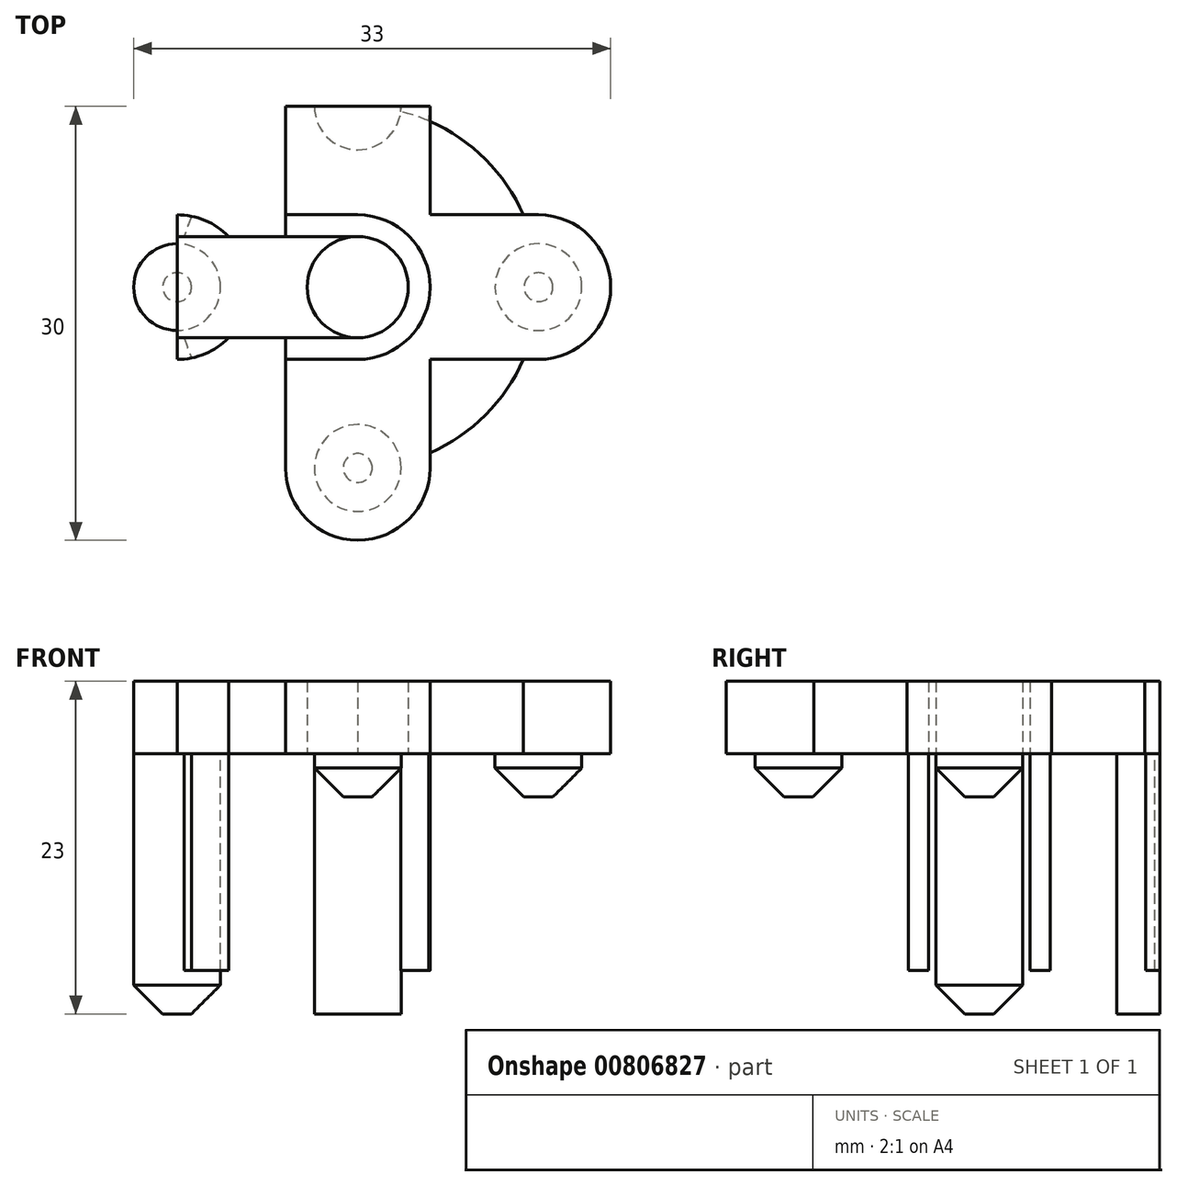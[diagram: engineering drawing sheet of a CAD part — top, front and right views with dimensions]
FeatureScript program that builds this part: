
annotation { "Feature Type Name" : "Feature", "Feature Type Description" : "" }
export const myFeature = defineFeature(function(context is Context, id is Id, definition is map)
    precondition{}
    {
        {
            var Q0;
            Q0=qCreatedBy(makeId("Top.planeOp"),FACE);
            var sketch = newSketch(context, id + "F0", { "sketchPlane" : qUnion([Q0])});
            skCircle(sketch, "E0", {"center": v(0, 0) * mm, "radius": 12.5 * mm});
            skCircle(sketch, "E1", {"center": v(0, 0) * mm, "radius": 3.5 * mm});
            skCircle(sketch, "E2", {"center": v(0, -12.5) * mm, "radius": 5 * mm});
            skCircle(sketch, "E3", {"center": v(0, 12.5) * mm, "radius": 5 * mm});
            skCircle(sketch, "E4", {"center": v(12.5, 0) * mm, "radius": 5 * mm});
            skCircle(sketch, "E5", {"center": v(-12.5, 0) * mm, "radius": 5 * mm});
            skCircle(sketch, "E6", {"center": v(-12.5, 0) * mm, "radius": 3 * mm});
            skCircle(sketch, "E7", {"center": v(0, 12.5) * mm, "radius": 3 * mm});
            skCircle(sketch, "E8", {"center": v(12.5, 0) * mm, "radius": 3 * mm});
            skCircle(sketch, "E9", {"center": v(0, -12.5) * mm, "radius": 3 * mm});
            skCircle(sketch, "E10", {"center": v(0, 0) * mm, "radius": 5 * mm});
            skLineSegment(sketch, "E11.bottom", {"start": v(0, 3.5) * mm, "end": v(-12.5, 3.5) * mm});
            skLineSegment(sketch, "E11.top", {"start": v(0, 5) * mm, "end": v(-12.5, 5) * mm});
            skLineSegment(sketch, "E11.left", {"start": v(0, 3.5) * mm, "end": v(0, 5) * mm});
            skLineSegment(sketch, "E11.right", {"start": v(-12.5, 3.5) * mm, "end": v(-12.5, 5) * mm});
            skLineSegment(sketch, "E12.bottom", {"start": v(0, -3.5) * mm, "end": v(-12.5, -3.5) * mm});
            skLineSegment(sketch, "E12.top", {"start": v(0, -5) * mm, "end": v(-12.5, -5) * mm});
            skLineSegment(sketch, "E12.left", {"start": v(0, -3.5) * mm, "end": v(0, -5) * mm});
            skLineSegment(sketch, "E12.right", {"start": v(-12.5, -3.5) * mm, "end": v(-12.5, -5) * mm});
            skLineSegment(sketch, "E13.bottom", {"start": v(5, 12.5) * mm, "end": v(-5, 12.5) * mm});
            skLineSegment(sketch, "E13.top", {"start": v(5, -12.5) * mm, "end": v(-5, -12.5) * mm});
            skLineSegment(sketch, "E13.left", {"start": v(5, 12.5) * mm, "end": v(5, -12.5) * mm});
            skLineSegment(sketch, "E13.right", {"start": v(-5, 12.5) * mm, "end": v(-5, -12.5) * mm});
            skLineSegment(sketch, "E14.bottom", {"start": v(12.5, 5) * mm, "end": v(-12.5, 5) * mm});
            skLineSegment(sketch, "E14.top", {"start": v(12.5, -5) * mm, "end": v(-12.5, -5) * mm});
            skLineSegment(sketch, "E14.left", {"start": v(12.5, 5) * mm, "end": v(12.5, -5) * mm});
            skLineSegment(sketch, "E14.right", {"start": v(-12.5, 5) * mm, "end": v(-12.5, -5) * mm});
            skSolve(sketch);
        }
        {
            var Q0;
            Q0=qCreatedBy(makeId("Front.planeOp"),FACE);
            var sketch = newSketch(context, id + "F1", { "sketchPlane" : qUnion([Q0])});
            skLineSegment(sketch, "E15", {"start": v(0, 0) * mm, "end": v(0, 10) * mm});
            skLineSegment(sketch, "E16", {"start": v(0, 10) * mm, "end": v(-12.5, 10) * mm});
            skLineSegment(sketch, "E17", {"start": v(-12.5, 10) * mm, "end": v(-12.5, 40) * mm});
            skLineSegment(sketch, "E18", {"start": v(-12.5, 40) * mm, "end": v(0, 10) * mm});
            skSolve(sketch);
        }
        {
            var Q0;
            Q0=makeQuery(id+"F1.imprint","IMPRINT",FACE,{"disambiguationData":[TD([[makeQuery(id+"F1.imprint","IMPRINT",EDGE,{"derivedFrom":sQuery(id+"F1.wireOp",EDGE,"E16")}),-1.0]])]});
            extrude(context, id + "F2", {"entities" : qUnion([Q0]), "endBound" : BoundingType.SYMMETRIC, "depth" : 10 * mm, "offsetDistance" : 25 * mm});
        }
        {
            var Q0;
            {var subQ0=sQuery(id+"F0.wireOp",EDGE,"E11.left");Q0=makeQuery(id+"F0.imprint","IMPRINT",FACE,{"disambiguationData":[TD([[makeQuery(id+"F0.imprint","IMPRINT",EDGE,{"derivedFrom":subQ0}),-1.0]])]});}
            var Q1;
            {var subQ0=sQuery(id+"F0.wireOp",EDGE,"E11.left");Q1=makeQuery(id+"F0.imprint","IMPRINT",FACE,{"disambiguationData":[TD([[makeQuery(id+"F0.imprint","IMPRINT",EDGE,{"derivedFrom":subQ0}),1.0]])]});}
            var Q2;
            {var subQ1=sQuery(id+"F0.wireOp",EDGE,"E10");var subQ3=sQuery(id+"F0.wireOp",EDGE,"E11.bottom");var subQ4=makeQuery(id+"F0.imprint","INTERSECT",VERTEX,{"derivedFrom":[subQ1,subQ3]});Q2=makeQuery(id+"F0.imprint","IMPRINT",FACE,{"disambiguationData":[TD([[makeQuery(id+"F0.imprint","IMPRINT",EDGE,{"disambiguationData":[TD([[subQ4,-1.0]])],"derivedFrom":subQ3}),-1.0]])]});}
            var Q3;
            {var subQ3=sQuery(id+"F0.wireOp",EDGE,"E14.bottom");var subQ7=sQuery(id+"F0.wireOp",EDGE,"E0");var subQ9=makeQuery(id+"F0.imprint","INTERSECT",VERTEX,{"disambiguationData":[OD(1.0)],"derivedFrom":[subQ7,subQ3]});Q3=makeQuery(id+"F0.imprint","IMPRINT",FACE,{"disambiguationData":[TD([[makeQuery(id+"F0.imprint","IMPRINT",EDGE,{"disambiguationData":[TD([[subQ9,-1.0]])],"derivedFrom":subQ7}),1.0]])]});}
            var Q4;
            {var subQ0=sQuery(id+"F0.wireOp",EDGE,"E5");var subQ1=sQuery(id+"F0.wireOp",EDGE,"E0");var subQ2=makeQuery(id+"F0.imprint","INTERSECT",VERTEX,{"disambiguationData":[OD(0.0)],"derivedFrom":[subQ1,subQ0]});Q4=makeQuery(id+"F0.imprint","IMPRINT",FACE,{"disambiguationData":[TD([[makeQuery(id+"F0.imprint","IMPRINT",EDGE,{"disambiguationData":[TD([[subQ2,-1.0]])],"derivedFrom":subQ1}),1.0]])]});}
            var Q5;
            {var subQ0=sQuery(id+"F0.wireOp",EDGE,"E5");var subQ1=sQuery(id+"F0.wireOp",EDGE,"E0");var subQ2=makeQuery(id+"F0.imprint","INTERSECT",VERTEX,{"disambiguationData":[OD(0.0)],"derivedFrom":[subQ1,subQ0]});Q5=makeQuery(id+"F0.imprint","IMPRINT",FACE,{"disambiguationData":[TD([[makeQuery(id+"F0.imprint","IMPRINT",EDGE,{"disambiguationData":[TD([[subQ2,-1.0]])],"derivedFrom":subQ1}),-1.0]])]});}
            var Q6;
            {var subQ0=sQuery(id+"F0.wireOp",EDGE,"E12.bottom");var subQ1=sQuery(id+"F0.wireOp",EDGE,"E0");var subQ2=makeQuery(id+"F0.imprint","INTERSECT",VERTEX,{"derivedFrom":[subQ1,subQ0]});Q6=makeQuery(id+"F0.imprint","IMPRINT",FACE,{"disambiguationData":[TD([[makeQuery(id+"F0.imprint","IMPRINT",EDGE,{"disambiguationData":[TD([[subQ2,-1.0]])],"derivedFrom":subQ1}),-1.0]])]});}
            var Q7;
            {var subQ0=sQuery(id+"F0.wireOp",EDGE,"E12.bottom");var subQ1=sQuery(id+"F0.wireOp",EDGE,"E0");var subQ2=makeQuery(id+"F0.imprint","INTERSECT",VERTEX,{"derivedFrom":[subQ1,subQ0]});Q7=makeQuery(id+"F0.imprint","IMPRINT",FACE,{"disambiguationData":[TD([[makeQuery(id+"F0.imprint","IMPRINT",EDGE,{"disambiguationData":[TD([[subQ2,-1.0]])],"derivedFrom":subQ1}),1.0]])]});}
            var Q8;
            {var subQ5=sQuery(id+"F0.wireOp",EDGE,"E14.top");var subQ7=sQuery(id+"F0.wireOp",EDGE,"E0");var subQ9=makeQuery(id+"F0.imprint","INTERSECT",VERTEX,{"disambiguationData":[OD(0.0)],"derivedFrom":[subQ7,subQ5]});Q8=makeQuery(id+"F0.imprint","IMPRINT",FACE,{"disambiguationData":[TD([[makeQuery(id+"F0.imprint","IMPRINT",EDGE,{"disambiguationData":[TD([[subQ9,1.0]])],"derivedFrom":subQ7}),1.0]])]});}
            var Q9;
            {var subQ1=sQuery(id+"F0.wireOp",EDGE,"E10");var subQ3=sQuery(id+"F0.wireOp",EDGE,"E12.bottom");var subQ4=makeQuery(id+"F0.imprint","INTERSECT",VERTEX,{"derivedFrom":[subQ1,subQ3]});Q9=makeQuery(id+"F0.imprint","IMPRINT",FACE,{"disambiguationData":[TD([[makeQuery(id+"F0.imprint","IMPRINT",EDGE,{"disambiguationData":[TD([[subQ4,-1.0]])],"derivedFrom":subQ3}),1.0]])]});}
            var Q10;
            {var subQ0=sQuery(id+"F0.wireOp",EDGE,"E12.left");Q10=makeQuery(id+"F0.imprint","IMPRINT",FACE,{"disambiguationData":[TD([[makeQuery(id+"F0.imprint","IMPRINT",EDGE,{"derivedFrom":subQ0}),-1.0]])]});}
            var Q11;
            {var subQ0=sQuery(id+"F0.wireOp",EDGE,"E14.top");var subQ1=sQuery(id+"F0.wireOp",EDGE,"E0");var subQ2=makeQuery(id+"F0.imprint","INTERSECT",VERTEX,{"disambiguationData":[OD(0.0)],"derivedFrom":[subQ1,subQ0]});Q11=makeQuery(id+"F0.imprint","IMPRINT",FACE,{"disambiguationData":[TD([[makeQuery(id+"F0.imprint","IMPRINT",EDGE,{"disambiguationData":[TD([[subQ2,1.0]])],"derivedFrom":subQ1}),-1.0]])]});}
            var Q12;
            {var subQ0=sQuery(id+"F0.wireOp",EDGE,"E14.bottom");var subQ1=sQuery(id+"F0.wireOp",EDGE,"E0");var subQ2=makeQuery(id+"F0.imprint","INTERSECT",VERTEX,{"disambiguationData":[OD(1.0)],"derivedFrom":[subQ1,subQ0]});Q12=makeQuery(id+"F0.imprint","IMPRINT",FACE,{"disambiguationData":[TD([[makeQuery(id+"F0.imprint","IMPRINT",EDGE,{"disambiguationData":[TD([[subQ2,-1.0]])],"derivedFrom":subQ1}),-1.0]])]});}
            var Q13;
            {var subQ0=sQuery(id+"F0.wireOp",EDGE,"E14.right");var subQ4=makeQuery(id+"F0.imprint","INTERSECT",VERTEX,{"derivedFrom":[sQuery(id+"F0.wireOp",EDGE,"E0"),subQ0]});Q13=makeQuery(id+"F0.imprint","IMPRINT",FACE,{"disambiguationData":[TD([[makeQuery(id+"F0.imprint","IMPRINT",EDGE,{"disambiguationData":[TD([[subQ4,1.0]])],"derivedFrom":subQ0}),-1.0]])]});}
            var Q14;
            {var subQ0=sQuery(id+"F0.wireOp",EDGE,"E14.right");var subQ1=sQuery(id+"F0.wireOp",EDGE,"E5");var subQ2=makeQuery(id+"F0.imprint","INTERSECT",VERTEX,{"derivedFrom":[subQ1,sQuery(id+"F0.wireOp",EDGE,"E14.bottom"),subQ0]});Q14=makeQuery(id+"F0.imprint","IMPRINT",FACE,{"disambiguationData":[TD([[makeQuery(id+"F0.imprint","IMPRINT",EDGE,{"disambiguationData":[TD([[subQ2,-1.0]])],"derivedFrom":subQ1}),1.0]])]});}
            extrude(context, id + "F3", {"entities" : qUnion([Q0, Q1, Q2, Q3, Q4, Q5, Q6, Q7, Q8, Q9, Q10, Q11, Q12, Q13, Q14]), "operationType" : NewBodyOperationType.ADD, "depth" : 40 * mm, "offsetDistance" : 25 * mm});
        }
        {
            var Q0;
            {var subQ0=sQuery(id+"F0.wireOp",EDGE,"E11.bottom");var subQ3=sQuery(id+"F0.wireOp",EDGE,"E10");var subQ4=makeQuery(id+"F0.imprint","INTERSECT",VERTEX,{"derivedFrom":[subQ3,subQ0]});Q0=makeQuery(id+"F0.imprint","IMPRINT",FACE,{"disambiguationData":[TD([[makeQuery(id+"F0.imprint","IMPRINT",EDGE,{"disambiguationData":[TD([[subQ4,-1.0]])],"derivedFrom":subQ3}),1.0]])]});}
            var Q1;
            {var subQ0=sQuery(id+"F0.wireOp",EDGE,"E11.bottom");var subQ1=sQuery(id+"F0.wireOp",EDGE,"E10");var subQ2=makeQuery(id+"F0.imprint","INTERSECT",VERTEX,{"derivedFrom":[subQ1,subQ0]});Q1=makeQuery(id+"F0.imprint","IMPRINT",FACE,{"disambiguationData":[TD([[makeQuery(id+"F0.imprint","IMPRINT",EDGE,{"disambiguationData":[TD([[subQ2,-1.0]])],"derivedFrom":subQ1}),-1.0]])]});}
            var Q2;
            {var subQ0=sQuery(id+"F0.wireOp",EDGE,"E13.right");var subQ1=sQuery(id+"F0.wireOp",EDGE,"E10");var subQ2=makeQuery(id+"F0.imprint","INTERSECT",VERTEX,{"derivedFrom":[subQ1,subQ0]});Q2=makeQuery(id+"F0.imprint","IMPRINT",FACE,{"disambiguationData":[TD([[makeQuery(id+"F0.imprint","IMPRINT",EDGE,{"disambiguationData":[TD([[subQ2,-1.0]])],"derivedFrom":subQ1}),-1.0]])]});}
            var Q3;
            {var subQ2=sQuery(id+"F0.wireOp",EDGE,"E11.bottom");var subQ5=sQuery(id+"F0.wireOp",EDGE,"E5");var subQ8=makeQuery(id+"F0.imprint","INTERSECT",VERTEX,{"derivedFrom":[subQ5,subQ2]});Q3=makeQuery(id+"F0.imprint","IMPRINT",FACE,{"disambiguationData":[TD([[makeQuery(id+"F0.imprint","IMPRINT",EDGE,{"disambiguationData":[TD([[subQ8,1.0]])],"derivedFrom":subQ5}),-1.0]])]});}
            var Q4;
            {var subQ0=sQuery(id+"F0.wireOp",EDGE,"E11.bottom");var subQ6=sQuery(id+"F0.wireOp",EDGE,"E0");var subQ10=makeQuery(id+"F0.imprint","INTERSECT",VERTEX,{"derivedFrom":[subQ6,subQ0]});Q4=makeQuery(id+"F0.imprint","IMPRINT",FACE,{"disambiguationData":[TD([[makeQuery(id+"F0.imprint","IMPRINT",EDGE,{"disambiguationData":[TD([[subQ10,-1.0]])],"derivedFrom":subQ6}),1.0]])]});}
            var Q5;
            {var subQ0=sQuery(id+"F0.wireOp",EDGE,"E6");var subQ1=sQuery(id+"F0.wireOp",EDGE,"E0");var subQ2=makeQuery(id+"F0.imprint","INTERSECT",VERTEX,{"disambiguationData":[OD(0.0)],"derivedFrom":[subQ1,subQ0]});Q5=makeQuery(id+"F0.imprint","IMPRINT",FACE,{"disambiguationData":[TD([[makeQuery(id+"F0.imprint","IMPRINT",EDGE,{"disambiguationData":[TD([[subQ2,-1.0]])],"derivedFrom":subQ1}),1.0]])]});}
            var Q6;
            {var subQ0=sQuery(id+"F0.wireOp",EDGE,"E6");var subQ1=sQuery(id+"F0.wireOp",EDGE,"E0");var subQ2=makeQuery(id+"F0.imprint","INTERSECT",VERTEX,{"disambiguationData":[OD(0.0)],"derivedFrom":[subQ1,subQ0]});Q6=makeQuery(id+"F0.imprint","IMPRINT",FACE,{"disambiguationData":[TD([[makeQuery(id+"F0.imprint","IMPRINT",EDGE,{"disambiguationData":[TD([[subQ2,-1.0]])],"derivedFrom":subQ1}),-1.0]])]});}
            var Q7;
            {var subQ0=sQuery(id+"F0.wireOp",EDGE,"E14.right");var subQ1=sQuery(id+"F0.wireOp",EDGE,"E0");var subQ2=makeQuery(id+"F0.imprint","INTERSECT",VERTEX,{"derivedFrom":[subQ1,subQ0]});Q7=makeQuery(id+"F0.imprint","IMPRINT",FACE,{"disambiguationData":[TD([[makeQuery(id+"F0.imprint","IMPRINT",EDGE,{"disambiguationData":[TD([[subQ2,-1.0]])],"derivedFrom":subQ1}),-1.0]])]});}
            var Q8;
            {var subQ0=sQuery(id+"F0.wireOp",EDGE,"E13.left");var subQ1=sQuery(id+"F0.wireOp",EDGE,"E0");var subQ2=makeQuery(id+"F0.imprint","INTERSECT",VERTEX,{"disambiguationData":[OD(0.0)],"derivedFrom":[subQ1,subQ0]});Q8=makeQuery(id+"F0.imprint","IMPRINT",FACE,{"disambiguationData":[TD([[makeQuery(id+"F0.imprint","IMPRINT",EDGE,{"disambiguationData":[TD([[subQ2,-1.0]])],"derivedFrom":subQ1}),1.0]])]});}
            var Q9;
            {var subQ0=sQuery(id+"F0.wireOp",EDGE,"E3");var subQ1=sQuery(id+"F0.wireOp",EDGE,"E0");var subQ2=makeQuery(id+"F0.imprint","INTERSECT",VERTEX,{"disambiguationData":[OD(0.0)],"derivedFrom":[subQ1,subQ0]});Q9=makeQuery(id+"F0.imprint","IMPRINT",FACE,{"disambiguationData":[TD([[makeQuery(id+"F0.imprint","IMPRINT",EDGE,{"disambiguationData":[TD([[subQ2,-1.0]])],"derivedFrom":subQ1}),1.0]])]});}
            var Q10;
            {var subQ0=sQuery(id+"F0.wireOp",EDGE,"E7");var subQ1=sQuery(id+"F0.wireOp",EDGE,"E0");var subQ2=makeQuery(id+"F0.imprint","INTERSECT",VERTEX,{"disambiguationData":[OD(0.0)],"derivedFrom":[subQ1,subQ0]});Q10=makeQuery(id+"F0.imprint","IMPRINT",FACE,{"disambiguationData":[TD([[makeQuery(id+"F0.imprint","IMPRINT",EDGE,{"disambiguationData":[TD([[subQ2,-1.0]])],"derivedFrom":subQ1}),1.0]])]});}
            var Q11;
            {var subQ0=sQuery(id+"F0.wireOp",EDGE,"E7");var subQ1=sQuery(id+"F0.wireOp",EDGE,"E0");var subQ2=makeQuery(id+"F0.imprint","INTERSECT",VERTEX,{"disambiguationData":[OD(0.0)],"derivedFrom":[subQ1,subQ0]});Q11=makeQuery(id+"F0.imprint","IMPRINT",FACE,{"disambiguationData":[TD([[makeQuery(id+"F0.imprint","IMPRINT",EDGE,{"disambiguationData":[TD([[subQ2,-1.0]])],"derivedFrom":subQ1}),-1.0]])]});}
            var Q12;
            {var subQ0=sQuery(id+"F0.wireOp",EDGE,"E3");var subQ1=sQuery(id+"F0.wireOp",EDGE,"E0");var subQ2=makeQuery(id+"F0.imprint","INTERSECT",VERTEX,{"disambiguationData":[OD(0.0)],"derivedFrom":[subQ1,subQ0]});Q12=makeQuery(id+"F0.imprint","IMPRINT",FACE,{"disambiguationData":[TD([[makeQuery(id+"F0.imprint","IMPRINT",EDGE,{"disambiguationData":[TD([[subQ2,-1.0]])],"derivedFrom":subQ1}),-1.0]])]});}
            var Q13;
            {var subQ0=sQuery(id+"F0.wireOp",EDGE,"E13.bottom");var subQ4=sQuery(id+"F0.wireOp",EDGE,"E7");var subQ5=makeQuery(id+"F0.imprint","INTERSECT",VERTEX,{"disambiguationData":[OD(0.0)],"derivedFrom":[subQ4,subQ0]});Q13=makeQuery(id+"F0.imprint","IMPRINT",FACE,{"disambiguationData":[TD([[makeQuery(id+"F0.imprint","IMPRINT",EDGE,{"disambiguationData":[TD([[subQ5,1.0]])],"derivedFrom":subQ4}),-1.0]])]});}
            var Q14;
            {var subQ0=sQuery(id+"F0.wireOp",EDGE,"E13.bottom");var subQ1=sQuery(id+"F0.wireOp",EDGE,"E7");var subQ2=makeQuery(id+"F0.imprint","INTERSECT",VERTEX,{"disambiguationData":[OD(0.0)],"derivedFrom":[subQ1,subQ0]});Q14=makeQuery(id+"F0.imprint","IMPRINT",FACE,{"disambiguationData":[TD([[makeQuery(id+"F0.imprint","IMPRINT",EDGE,{"disambiguationData":[TD([[subQ2,1.0]])],"derivedFrom":subQ1}),1.0]])]});}
            var Q15;
            {var subQ0=sQuery(id+"F0.wireOp",EDGE,"E13.bottom");var subQ1=sQuery(id+"F0.wireOp",EDGE,"E0");var subQ2=makeQuery(id+"F0.imprint","INTERSECT",VERTEX,{"derivedFrom":[subQ1,subQ0]});Q15=makeQuery(id+"F0.imprint","IMPRINT",FACE,{"disambiguationData":[TD([[makeQuery(id+"F0.imprint","IMPRINT",EDGE,{"disambiguationData":[TD([[subQ2,-1.0]])],"derivedFrom":subQ1}),-1.0]])]});}
            var Q16;
            {var subQ0=sQuery(id+"F0.wireOp",EDGE,"E7");var subQ1=sQuery(id+"F0.wireOp",EDGE,"E0");var subQ2=makeQuery(id+"F0.imprint","INTERSECT",VERTEX,{"disambiguationData":[OD(1.0)],"derivedFrom":[subQ1,subQ0]});Q16=makeQuery(id+"F0.imprint","IMPRINT",FACE,{"disambiguationData":[TD([[makeQuery(id+"F0.imprint","IMPRINT",EDGE,{"disambiguationData":[TD([[subQ2,-1.0]])],"derivedFrom":subQ1}),-1.0]])]});}
            var Q17;
            {var subQ0=sQuery(id+"F0.wireOp",EDGE,"E8");var subQ1=sQuery(id+"F0.wireOp",EDGE,"E0");var subQ2=makeQuery(id+"F0.imprint","INTERSECT",VERTEX,{"disambiguationData":[OD(0.0)],"derivedFrom":[subQ1,subQ0]});Q17=makeQuery(id+"F0.imprint","IMPRINT",FACE,{"disambiguationData":[TD([[makeQuery(id+"F0.imprint","IMPRINT",EDGE,{"disambiguationData":[TD([[subQ2,-1.0]])],"derivedFrom":subQ1}),1.0]])]});}
            var Q18;
            {var subQ0=sQuery(id+"F0.wireOp",EDGE,"E8");var subQ1=sQuery(id+"F0.wireOp",EDGE,"E0");var subQ2=makeQuery(id+"F0.imprint","INTERSECT",VERTEX,{"disambiguationData":[OD(0.0)],"derivedFrom":[subQ1,subQ0]});Q18=makeQuery(id+"F0.imprint","IMPRINT",FACE,{"disambiguationData":[TD([[makeQuery(id+"F0.imprint","IMPRINT",EDGE,{"disambiguationData":[TD([[subQ2,-1.0]])],"derivedFrom":subQ1}),-1.0]])]});}
            var Q19;
            {var subQ0=sQuery(id+"F0.wireOp",EDGE,"E14.left");var subQ4=sQuery(id+"F0.wireOp",EDGE,"E8");var subQ5=makeQuery(id+"F0.imprint","INTERSECT",VERTEX,{"disambiguationData":[OD(0.0)],"derivedFrom":[subQ4,subQ0]});Q19=makeQuery(id+"F0.imprint","IMPRINT",FACE,{"disambiguationData":[TD([[makeQuery(id+"F0.imprint","IMPRINT",EDGE,{"disambiguationData":[TD([[subQ5,1.0]])],"derivedFrom":subQ4}),-1.0]])]});}
            var Q20;
            {var subQ0=sQuery(id+"F0.wireOp",EDGE,"E14.left");var subQ1=sQuery(id+"F0.wireOp",EDGE,"E8");var subQ2=makeQuery(id+"F0.imprint","INTERSECT",VERTEX,{"disambiguationData":[OD(0.0)],"derivedFrom":[subQ1,subQ0]});Q20=makeQuery(id+"F0.imprint","IMPRINT",FACE,{"disambiguationData":[TD([[makeQuery(id+"F0.imprint","IMPRINT",EDGE,{"disambiguationData":[TD([[subQ2,1.0]])],"derivedFrom":subQ1}),1.0]])]});}
            var Q21;
            {var subQ0=sQuery(id+"F0.wireOp",EDGE,"E8");var subQ1=sQuery(id+"F0.wireOp",EDGE,"E0");var subQ2=makeQuery(id+"F0.imprint","INTERSECT",VERTEX,{"disambiguationData":[OD(0.0)],"derivedFrom":[subQ1,subQ0]});Q21=makeQuery(id+"F0.imprint","IMPRINT",FACE,{"disambiguationData":[TD([[makeQuery(id+"F0.imprint","IMPRINT",EDGE,{"disambiguationData":[TD([[subQ2,1.0]])],"derivedFrom":subQ1}),1.0]])]});}
            var Q22;
            {var subQ0=sQuery(id+"F0.wireOp",EDGE,"E8");var subQ1=sQuery(id+"F0.wireOp",EDGE,"E0");var subQ2=makeQuery(id+"F0.imprint","INTERSECT",VERTEX,{"disambiguationData":[OD(0.0)],"derivedFrom":[subQ1,subQ0]});Q22=makeQuery(id+"F0.imprint","IMPRINT",FACE,{"disambiguationData":[TD([[makeQuery(id+"F0.imprint","IMPRINT",EDGE,{"disambiguationData":[TD([[subQ2,1.0]])],"derivedFrom":subQ1}),-1.0]])]});}
            var Q23;
            {var subQ0=sQuery(id+"F0.wireOp",EDGE,"E14.left");var subQ1=sQuery(id+"F0.wireOp",EDGE,"E0");var subQ2=makeQuery(id+"F0.imprint","INTERSECT",VERTEX,{"derivedFrom":[subQ1,subQ0]});Q23=makeQuery(id+"F0.imprint","IMPRINT",FACE,{"disambiguationData":[TD([[makeQuery(id+"F0.imprint","IMPRINT",EDGE,{"disambiguationData":[TD([[subQ2,1.0]])],"derivedFrom":subQ1}),-1.0]])]});}
            var Q24;
            {var subQ0=sQuery(id+"F0.wireOp",EDGE,"E4");var subQ1=sQuery(id+"F0.wireOp",EDGE,"E0");var subQ2=makeQuery(id+"F0.imprint","INTERSECT",VERTEX,{"disambiguationData":[OD(1.0)],"derivedFrom":[subQ1,subQ0]});Q24=makeQuery(id+"F0.imprint","IMPRINT",FACE,{"disambiguationData":[TD([[makeQuery(id+"F0.imprint","IMPRINT",EDGE,{"disambiguationData":[TD([[subQ2,-1.0]])],"derivedFrom":subQ1}),-1.0]])]});}
            var Q25;
            {var subQ2=sQuery(id+"F0.wireOp",EDGE,"E14.bottom");var subQ5=sQuery(id+"F0.wireOp",EDGE,"E0");var subQ8=makeQuery(id+"F0.imprint","INTERSECT",VERTEX,{"disambiguationData":[OD(0.0)],"derivedFrom":[subQ5,subQ2]});Q25=makeQuery(id+"F0.imprint","IMPRINT",FACE,{"disambiguationData":[TD([[makeQuery(id+"F0.imprint","IMPRINT",EDGE,{"disambiguationData":[TD([[subQ8,1.0]])],"derivedFrom":subQ5}),1.0]])]});}
            var Q26;
            {var subQ0=sQuery(id+"F0.wireOp",EDGE,"E13.left");var subQ1=sQuery(id+"F0.wireOp",EDGE,"E0");var subQ2=makeQuery(id+"F0.imprint","INTERSECT",VERTEX,{"disambiguationData":[OD(0.0)],"derivedFrom":[subQ1,subQ0]});Q26=makeQuery(id+"F0.imprint","IMPRINT",FACE,{"disambiguationData":[TD([[makeQuery(id+"F0.imprint","IMPRINT",EDGE,{"disambiguationData":[TD([[subQ2,-1.0]])],"derivedFrom":subQ1}),-1.0]])]});}
            var Q27;
            {var subQ0=sQuery(id+"F0.wireOp",EDGE,"E13.right");var subQ1=sQuery(id+"F0.wireOp",EDGE,"E0");var subQ2=makeQuery(id+"F0.imprint","INTERSECT",VERTEX,{"disambiguationData":[OD(0.0)],"derivedFrom":[subQ1,subQ0]});Q27=makeQuery(id+"F0.imprint","IMPRINT",FACE,{"disambiguationData":[TD([[makeQuery(id+"F0.imprint","IMPRINT",EDGE,{"disambiguationData":[TD([[subQ2,1.0]])],"derivedFrom":subQ1}),-1.0]])]});}
            var Q28;
            {var subQ0=sQuery(id+"F0.wireOp",EDGE,"E14.bottom");var subQ1=sQuery(id+"F0.wireOp",EDGE,"E0");var subQ2=makeQuery(id+"F0.imprint","INTERSECT",VERTEX,{"disambiguationData":[OD(0.0)],"derivedFrom":[subQ1,subQ0]});Q28=makeQuery(id+"F0.imprint","IMPRINT",FACE,{"disambiguationData":[TD([[makeQuery(id+"F0.imprint","IMPRINT",EDGE,{"disambiguationData":[TD([[subQ2,1.0]])],"derivedFrom":subQ1}),-1.0]])]});}
            var Q29;
            {var subQ0=sQuery(id+"F0.wireOp",EDGE,"E14.top");var subQ1=sQuery(id+"F0.wireOp",EDGE,"E0");var subQ2=makeQuery(id+"F0.imprint","INTERSECT",VERTEX,{"disambiguationData":[OD(1.0)],"derivedFrom":[subQ1,subQ0]});Q29=makeQuery(id+"F0.imprint","IMPRINT",FACE,{"disambiguationData":[TD([[makeQuery(id+"F0.imprint","IMPRINT",EDGE,{"disambiguationData":[TD([[subQ2,-1.0]])],"derivedFrom":subQ1}),-1.0]])]});}
            var Q30;
            {var subQ0=sQuery(id+"F0.wireOp",EDGE,"E13.top");var subQ4=sQuery(id+"F0.wireOp",EDGE,"E9");var subQ5=makeQuery(id+"F0.imprint","INTERSECT",VERTEX,{"disambiguationData":[OD(0.0)],"derivedFrom":[subQ4,subQ0]});Q30=makeQuery(id+"F0.imprint","IMPRINT",FACE,{"disambiguationData":[TD([[makeQuery(id+"F0.imprint","IMPRINT",EDGE,{"disambiguationData":[TD([[subQ5,1.0]])],"derivedFrom":subQ4}),-1.0]])]});}
            var Q31;
            {var subQ0=sQuery(id+"F0.wireOp",EDGE,"E13.top");var subQ1=sQuery(id+"F0.wireOp",EDGE,"E0");var subQ2=makeQuery(id+"F0.imprint","INTERSECT",VERTEX,{"derivedFrom":[subQ1,subQ0]});Q31=makeQuery(id+"F0.imprint","IMPRINT",FACE,{"disambiguationData":[TD([[makeQuery(id+"F0.imprint","IMPRINT",EDGE,{"disambiguationData":[TD([[subQ2,-1.0]])],"derivedFrom":subQ1}),-1.0]])]});}
            var Q32;
            {var subQ0=sQuery(id+"F0.wireOp",EDGE,"E9");var subQ1=sQuery(id+"F0.wireOp",EDGE,"E0");var subQ2=makeQuery(id+"F0.imprint","INTERSECT",VERTEX,{"disambiguationData":[OD(1.0)],"derivedFrom":[subQ1,subQ0]});Q32=makeQuery(id+"F0.imprint","IMPRINT",FACE,{"disambiguationData":[TD([[makeQuery(id+"F0.imprint","IMPRINT",EDGE,{"disambiguationData":[TD([[subQ2,-1.0]])],"derivedFrom":subQ1}),-1.0]])]});}
            var Q33;
            {var subQ0=sQuery(id+"F0.wireOp",EDGE,"E13.top");var subQ1=sQuery(id+"F0.wireOp",EDGE,"E9");var subQ2=makeQuery(id+"F0.imprint","INTERSECT",VERTEX,{"disambiguationData":[OD(0.0)],"derivedFrom":[subQ1,subQ0]});Q33=makeQuery(id+"F0.imprint","IMPRINT",FACE,{"disambiguationData":[TD([[makeQuery(id+"F0.imprint","IMPRINT",EDGE,{"disambiguationData":[TD([[subQ2,1.0]])],"derivedFrom":subQ1}),1.0]])]});}
            var Q34;
            {var subQ0=sQuery(id+"F0.wireOp",EDGE,"E9");var subQ1=sQuery(id+"F0.wireOp",EDGE,"E0");var subQ2=makeQuery(id+"F0.imprint","INTERSECT",VERTEX,{"disambiguationData":[OD(0.0)],"derivedFrom":[subQ1,subQ0]});Q34=makeQuery(id+"F0.imprint","IMPRINT",FACE,{"disambiguationData":[TD([[makeQuery(id+"F0.imprint","IMPRINT",EDGE,{"disambiguationData":[TD([[subQ2,-1.0]])],"derivedFrom":subQ1}),1.0]])]});}
            var Q35;
            {var subQ0=sQuery(id+"F0.wireOp",EDGE,"E2");var subQ1=sQuery(id+"F0.wireOp",EDGE,"E0");var subQ2=makeQuery(id+"F0.imprint","INTERSECT",VERTEX,{"disambiguationData":[OD(0.0)],"derivedFrom":[subQ1,subQ0]});Q35=makeQuery(id+"F0.imprint","IMPRINT",FACE,{"disambiguationData":[TD([[makeQuery(id+"F0.imprint","IMPRINT",EDGE,{"disambiguationData":[TD([[subQ2,-1.0]])],"derivedFrom":subQ1}),1.0]])]});}
            var Q36;
            {var subQ0=sQuery(id+"F0.wireOp",EDGE,"E2");var subQ1=sQuery(id+"F0.wireOp",EDGE,"E0");var subQ2=makeQuery(id+"F0.imprint","INTERSECT",VERTEX,{"disambiguationData":[OD(0.0)],"derivedFrom":[subQ1,subQ0]});Q36=makeQuery(id+"F0.imprint","IMPRINT",FACE,{"disambiguationData":[TD([[makeQuery(id+"F0.imprint","IMPRINT",EDGE,{"disambiguationData":[TD([[subQ2,-1.0]])],"derivedFrom":subQ1}),-1.0]])]});}
            var Q37;
            {var subQ0=sQuery(id+"F0.wireOp",EDGE,"E9");var subQ1=sQuery(id+"F0.wireOp",EDGE,"E0");var subQ2=makeQuery(id+"F0.imprint","INTERSECT",VERTEX,{"disambiguationData":[OD(0.0)],"derivedFrom":[subQ1,subQ0]});Q37=makeQuery(id+"F0.imprint","IMPRINT",FACE,{"disambiguationData":[TD([[makeQuery(id+"F0.imprint","IMPRINT",EDGE,{"disambiguationData":[TD([[subQ2,-1.0]])],"derivedFrom":subQ1}),-1.0]])]});}
            var Q38;
            {var subQ1=sQuery(id+"F0.wireOp",EDGE,"E0");var subQ8=sQuery(id+"F0.wireOp",EDGE,"E13.right");var subQ9=makeQuery(id+"F0.imprint","INTERSECT",VERTEX,{"disambiguationData":[OD(1.0)],"derivedFrom":[subQ1,subQ8]});Q38=makeQuery(id+"F0.imprint","IMPRINT",FACE,{"disambiguationData":[TD([[makeQuery(id+"F0.imprint","IMPRINT",EDGE,{"disambiguationData":[TD([[subQ9,-1.0]])],"derivedFrom":subQ1}),1.0]])]});}
            var Q39;
            {var subQ0=sQuery(id+"F0.wireOp",EDGE,"E13.left");var subQ1=sQuery(id+"F0.wireOp",EDGE,"E0");var subQ2=makeQuery(id+"F0.imprint","INTERSECT",VERTEX,{"disambiguationData":[OD(1.0)],"derivedFrom":[subQ1,subQ0]});Q39=makeQuery(id+"F0.imprint","IMPRINT",FACE,{"disambiguationData":[TD([[makeQuery(id+"F0.imprint","IMPRINT",EDGE,{"disambiguationData":[TD([[subQ2,1.0]])],"derivedFrom":subQ1}),-1.0]])]});}
            var Q40;
            {var subQ0=sQuery(id+"F0.wireOp",EDGE,"E13.right");var subQ1=sQuery(id+"F0.wireOp",EDGE,"E0");var subQ2=makeQuery(id+"F0.imprint","INTERSECT",VERTEX,{"disambiguationData":[OD(1.0)],"derivedFrom":[subQ1,subQ0]});Q40=makeQuery(id+"F0.imprint","IMPRINT",FACE,{"disambiguationData":[TD([[makeQuery(id+"F0.imprint","IMPRINT",EDGE,{"disambiguationData":[TD([[subQ2,-1.0]])],"derivedFrom":subQ1}),-1.0]])]});}
            var Q41;
            {var subQ1=sQuery(id+"F0.wireOp",EDGE,"E10");var subQ3=sQuery(id+"F0.wireOp",EDGE,"E13.left");var subQ4=makeQuery(id+"F0.imprint","INTERSECT",VERTEX,{"derivedFrom":[subQ1,subQ3]});Q41=makeQuery(id+"F0.imprint","IMPRINT",FACE,{"disambiguationData":[TD([[makeQuery(id+"F0.imprint","IMPRINT",EDGE,{"disambiguationData":[TD([[subQ4,1.0]])],"derivedFrom":subQ3}),-1.0]])]});}
            var Q42;
            {var subQ1=sQuery(id+"F0.wireOp",EDGE,"E10");var subQ3=sQuery(id+"F0.wireOp",EDGE,"E13.left");var subQ4=makeQuery(id+"F0.imprint","INTERSECT",VERTEX,{"derivedFrom":[subQ1,subQ3]});Q42=makeQuery(id+"F0.imprint","IMPRINT",FACE,{"disambiguationData":[TD([[makeQuery(id+"F0.imprint","IMPRINT",EDGE,{"disambiguationData":[TD([[subQ4,-1.0]])],"derivedFrom":subQ3}),-1.0]])]});}
            var Q43;
            {var subQ0=sQuery(id+"F0.wireOp",EDGE,"E6");var subQ1=sQuery(id+"F0.wireOp",EDGE,"E0");var subQ2=makeQuery(id+"F0.imprint","INTERSECT",VERTEX,{"disambiguationData":[OD(1.0)],"derivedFrom":[subQ1,subQ0]});Q43=makeQuery(id+"F0.imprint","IMPRINT",FACE,{"disambiguationData":[TD([[makeQuery(id+"F0.imprint","IMPRINT",EDGE,{"disambiguationData":[TD([[subQ2,-1.0]])],"derivedFrom":subQ1}),-1.0]])]});}
            var Q44;
            {var subQ0=sQuery(id+"F0.wireOp",EDGE,"E11.bottom");var subQ1=sQuery(id+"F0.wireOp",EDGE,"E0");var subQ2=makeQuery(id+"F0.imprint","INTERSECT",VERTEX,{"derivedFrom":[subQ1,subQ0]});Q44=makeQuery(id+"F0.imprint","IMPRINT",FACE,{"disambiguationData":[TD([[makeQuery(id+"F0.imprint","IMPRINT",EDGE,{"disambiguationData":[TD([[subQ2,-1.0]])],"derivedFrom":subQ1}),-1.0]])]});}
            extrude(context, id + "F4", {"entities" : qUnion([Q0, Q1, Q2, Q3, Q4, Q5, Q6, Q7, Q8, Q9, Q10, Q11, Q12, Q13, Q14, Q15, Q16, Q17, Q18, Q19, Q20, Q21, Q22, Q23, Q24, Q25, Q26, Q27, Q28, Q29, Q30, Q31, Q32, Q33, Q34, Q35, Q36, Q37, Q38, Q39, Q40, Q41, Q42, Q43, Q44]), "depth" : 10 * mm, "offsetDistance" : 25 * mm});
        }
        {
            var Q0;
            {var subQ0=sQuery(id+"F0.wireOp",EDGE,"E1");var subQ1=makeQuery(id+"F0.imprint","INTERSECT",VERTEX,{"derivedFrom":[subQ0,sQuery(id+"F0.wireOp",EDGE,"E11.bottom"),sQuery(id+"F0.wireOp",EDGE,"E11.left")]});Q0=makeQuery(id+"F0.imprint","IMPRINT",FACE,{"disambiguationData":[TD([[makeQuery(id+"F0.imprint","IMPRINT",EDGE,{"disambiguationData":[TD([[subQ1,-1.0]])],"derivedFrom":subQ0}),1.0]])]});}
            extrude(context, id + "F5", {"entities" : qUnion([Q0]), "operationType" : NewBodyOperationType.REMOVE, "oppositeDirection" : true, "depth" : -40 * mm, "offsetDistance" : 25 * mm});
        }
        {
            var Q0;
            {var subQ0=sQuery(id+"F0.wireOp",EDGE,"E14.right");var subQ1=sQuery(id+"F0.wireOp",EDGE,"E5");var subQ2=makeQuery(id+"F0.imprint","INTERSECT",VERTEX,{"derivedFrom":[subQ1,sQuery(id+"F0.wireOp",EDGE,"E14.bottom"),subQ0]});Q0=makeQuery(id+"F0.imprint","IMPRINT",FACE,{"disambiguationData":[TD([[makeQuery(id+"F0.imprint","IMPRINT",EDGE,{"disambiguationData":[TD([[subQ2,-1.0]])],"derivedFrom":subQ1}),1.0]])]});}
            var Q1;
            {var subQ0=sQuery(id+"F0.wireOp",EDGE,"E13.bottom");var subQ4=sQuery(id+"F0.wireOp",EDGE,"E7");var subQ5=makeQuery(id+"F0.imprint","INTERSECT",VERTEX,{"disambiguationData":[OD(0.0)],"derivedFrom":[subQ4,subQ0]});Q1=makeQuery(id+"F0.imprint","IMPRINT",FACE,{"disambiguationData":[TD([[makeQuery(id+"F0.imprint","IMPRINT",EDGE,{"disambiguationData":[TD([[subQ5,1.0]])],"derivedFrom":subQ4}),-1.0]])]});}
            extrude(context, id + "F6", {"entities" : qUnion([Q0, Q1]), "oppositeDirection" : true, "depth" : 15 * mm, "offsetDistance" : 25 * mm});
        }
        {
            var Q0;
            {var subQ0=sQuery(id+"F0.wireOp",EDGE,"E14.right");var subQ4=makeQuery(id+"F0.imprint","INTERSECT",VERTEX,{"derivedFrom":[sQuery(id+"F0.wireOp",EDGE,"E0"),subQ0]});Q0=makeQuery(id+"F0.imprint","IMPRINT",FACE,{"disambiguationData":[TD([[makeQuery(id+"F0.imprint","IMPRINT",EDGE,{"disambiguationData":[TD([[subQ4,1.0]])],"derivedFrom":subQ0}),-1.0]])]});}
            var Q1;
            {var subQ0=sQuery(id+"F0.wireOp",EDGE,"E14.right");var subQ1=sQuery(id+"F0.wireOp",EDGE,"E0");var subQ2=makeQuery(id+"F0.imprint","INTERSECT",VERTEX,{"derivedFrom":[subQ1,subQ0]});Q1=makeQuery(id+"F0.imprint","IMPRINT",FACE,{"disambiguationData":[TD([[makeQuery(id+"F0.imprint","IMPRINT",EDGE,{"disambiguationData":[TD([[subQ2,-1.0]])],"derivedFrom":subQ1}),-1.0]])]});}
            var Q2;
            {var subQ0=sQuery(id+"F0.wireOp",EDGE,"E6");var subQ1=sQuery(id+"F0.wireOp",EDGE,"E0");var subQ2=makeQuery(id+"F0.imprint","INTERSECT",VERTEX,{"disambiguationData":[OD(0.0)],"derivedFrom":[subQ1,subQ0]});Q2=makeQuery(id+"F0.imprint","IMPRINT",FACE,{"disambiguationData":[TD([[makeQuery(id+"F0.imprint","IMPRINT",EDGE,{"disambiguationData":[TD([[subQ2,-1.0]])],"derivedFrom":subQ1}),1.0]])]});}
            var Q3;
            {var subQ0=sQuery(id+"F0.wireOp",EDGE,"E6");var subQ1=sQuery(id+"F0.wireOp",EDGE,"E0");var subQ2=makeQuery(id+"F0.imprint","INTERSECT",VERTEX,{"disambiguationData":[OD(0.0)],"derivedFrom":[subQ1,subQ0]});Q3=makeQuery(id+"F0.imprint","IMPRINT",FACE,{"disambiguationData":[TD([[makeQuery(id+"F0.imprint","IMPRINT",EDGE,{"disambiguationData":[TD([[subQ2,-1.0]])],"derivedFrom":subQ1}),-1.0]])]});}
            var Q4;
            {var subQ0=sQuery(id+"F0.wireOp",EDGE,"E7");var subQ1=sQuery(id+"F0.wireOp",EDGE,"E0");var subQ2=makeQuery(id+"F0.imprint","INTERSECT",VERTEX,{"disambiguationData":[OD(0.0)],"derivedFrom":[subQ1,subQ0]});Q4=makeQuery(id+"F0.imprint","IMPRINT",FACE,{"disambiguationData":[TD([[makeQuery(id+"F0.imprint","IMPRINT",EDGE,{"disambiguationData":[TD([[subQ2,-1.0]])],"derivedFrom":subQ1}),1.0]])]});}
            var Q5;
            {var subQ0=sQuery(id+"F0.wireOp",EDGE,"E7");var subQ1=sQuery(id+"F0.wireOp",EDGE,"E0");var subQ2=makeQuery(id+"F0.imprint","INTERSECT",VERTEX,{"disambiguationData":[OD(0.0)],"derivedFrom":[subQ1,subQ0]});Q5=makeQuery(id+"F0.imprint","IMPRINT",FACE,{"disambiguationData":[TD([[makeQuery(id+"F0.imprint","IMPRINT",EDGE,{"disambiguationData":[TD([[subQ2,-1.0]])],"derivedFrom":subQ1}),-1.0]])]});}
            var Q6;
            {var subQ0=sQuery(id+"F0.wireOp",EDGE,"E13.bottom");var subQ1=sQuery(id+"F0.wireOp",EDGE,"E0");var subQ2=makeQuery(id+"F0.imprint","INTERSECT",VERTEX,{"derivedFrom":[subQ1,subQ0]});Q6=makeQuery(id+"F0.imprint","IMPRINT",FACE,{"disambiguationData":[TD([[makeQuery(id+"F0.imprint","IMPRINT",EDGE,{"disambiguationData":[TD([[subQ2,-1.0]])],"derivedFrom":subQ1}),-1.0]])]});}
            var Q7;
            {var subQ0=sQuery(id+"F0.wireOp",EDGE,"E13.bottom");var subQ1=sQuery(id+"F0.wireOp",EDGE,"E7");var subQ2=makeQuery(id+"F0.imprint","INTERSECT",VERTEX,{"disambiguationData":[OD(0.0)],"derivedFrom":[subQ1,subQ0]});Q7=makeQuery(id+"F0.imprint","IMPRINT",FACE,{"disambiguationData":[TD([[makeQuery(id+"F0.imprint","IMPRINT",EDGE,{"disambiguationData":[TD([[subQ2,1.0]])],"derivedFrom":subQ1}),1.0]])]});}
            extrude(context, id + "F7", {"entities" : qUnion([Q0, Q1, Q2, Q3, Q4, Q5, Q6, Q7]), "oppositeDirection" : true, "depth" : 18 * mm, "offsetDistance" : 25 * mm});
        }
        {
            var Q0;
            Q0=makeQuery(id+"F7.opExtrude","CAP_FACE",FACE,{"disambiguationData":[OSD([sQuery(id+"F0.wireOp",EDGE,"E6")])],"isStart":false});
            var Q1;
            Q1=makeQuery(id+"F7.opExtrude","CAP_FACE",FACE,{"disambiguationData":[OSD([sQuery(id+"F0.wireOp",EDGE,"E7")])],"isStart":false});
            chamfer(context, id + "F8", {"entities" : qUnion([Q0, Q1]), "width" : 2 * mm, "tangentPropagation" : true});
        }
        {
            var Q0;
            {var subQ0=sQuery(id+"F0.wireOp",EDGE,"E14.left");var subQ1=sQuery(id+"F0.wireOp",EDGE,"E0");var subQ2=makeQuery(id+"F0.imprint","INTERSECT",VERTEX,{"derivedFrom":[subQ1,subQ0]});Q0=makeQuery(id+"F0.imprint","IMPRINT",FACE,{"disambiguationData":[TD([[makeQuery(id+"F0.imprint","IMPRINT",EDGE,{"disambiguationData":[TD([[subQ2,1.0]])],"derivedFrom":subQ1}),-1.0]])]});}
            var Q1;
            {var subQ0=sQuery(id+"F0.wireOp",EDGE,"E8");var subQ1=sQuery(id+"F0.wireOp",EDGE,"E0");var subQ2=makeQuery(id+"F0.imprint","INTERSECT",VERTEX,{"disambiguationData":[OD(0.0)],"derivedFrom":[subQ1,subQ0]});Q1=makeQuery(id+"F0.imprint","IMPRINT",FACE,{"disambiguationData":[TD([[makeQuery(id+"F0.imprint","IMPRINT",EDGE,{"disambiguationData":[TD([[subQ2,1.0]])],"derivedFrom":subQ1}),1.0]])]});}
            var Q2;
            {var subQ0=sQuery(id+"F0.wireOp",EDGE,"E8");var subQ1=sQuery(id+"F0.wireOp",EDGE,"E0");var subQ2=makeQuery(id+"F0.imprint","INTERSECT",VERTEX,{"disambiguationData":[OD(0.0)],"derivedFrom":[subQ1,subQ0]});Q2=makeQuery(id+"F0.imprint","IMPRINT",FACE,{"disambiguationData":[TD([[makeQuery(id+"F0.imprint","IMPRINT",EDGE,{"disambiguationData":[TD([[subQ2,1.0]])],"derivedFrom":subQ1}),-1.0]])]});}
            var Q3;
            {var subQ0=sQuery(id+"F0.wireOp",EDGE,"E14.left");var subQ1=sQuery(id+"F0.wireOp",EDGE,"E8");var subQ2=makeQuery(id+"F0.imprint","INTERSECT",VERTEX,{"disambiguationData":[OD(0.0)],"derivedFrom":[subQ1,subQ0]});Q3=makeQuery(id+"F0.imprint","IMPRINT",FACE,{"disambiguationData":[TD([[makeQuery(id+"F0.imprint","IMPRINT",EDGE,{"disambiguationData":[TD([[subQ2,1.0]])],"derivedFrom":subQ1}),1.0]])]});}
            var Q4;
            {var subQ0=sQuery(id+"F0.wireOp",EDGE,"E13.top");var subQ1=sQuery(id+"F0.wireOp",EDGE,"E9");var subQ2=makeQuery(id+"F0.imprint","INTERSECT",VERTEX,{"disambiguationData":[OD(0.0)],"derivedFrom":[subQ1,subQ0]});Q4=makeQuery(id+"F0.imprint","IMPRINT",FACE,{"disambiguationData":[TD([[makeQuery(id+"F0.imprint","IMPRINT",EDGE,{"disambiguationData":[TD([[subQ2,1.0]])],"derivedFrom":subQ1}),1.0]])]});}
            var Q5;
            {var subQ0=sQuery(id+"F0.wireOp",EDGE,"E9");var subQ1=sQuery(id+"F0.wireOp",EDGE,"E0");var subQ2=makeQuery(id+"F0.imprint","INTERSECT",VERTEX,{"disambiguationData":[OD(0.0)],"derivedFrom":[subQ1,subQ0]});Q5=makeQuery(id+"F0.imprint","IMPRINT",FACE,{"disambiguationData":[TD([[makeQuery(id+"F0.imprint","IMPRINT",EDGE,{"disambiguationData":[TD([[subQ2,-1.0]])],"derivedFrom":subQ1}),1.0]])]});}
            var Q6;
            {var subQ0=sQuery(id+"F0.wireOp",EDGE,"E13.top");var subQ1=sQuery(id+"F0.wireOp",EDGE,"E0");var subQ2=makeQuery(id+"F0.imprint","INTERSECT",VERTEX,{"derivedFrom":[subQ1,subQ0]});Q6=makeQuery(id+"F0.imprint","IMPRINT",FACE,{"disambiguationData":[TD([[makeQuery(id+"F0.imprint","IMPRINT",EDGE,{"disambiguationData":[TD([[subQ2,-1.0]])],"derivedFrom":subQ1}),-1.0]])]});}
            var Q7;
            {var subQ0=sQuery(id+"F0.wireOp",EDGE,"E9");var subQ1=sQuery(id+"F0.wireOp",EDGE,"E0");var subQ2=makeQuery(id+"F0.imprint","INTERSECT",VERTEX,{"disambiguationData":[OD(0.0)],"derivedFrom":[subQ1,subQ0]});Q7=makeQuery(id+"F0.imprint","IMPRINT",FACE,{"disambiguationData":[TD([[makeQuery(id+"F0.imprint","IMPRINT",EDGE,{"disambiguationData":[TD([[subQ2,-1.0]])],"derivedFrom":subQ1}),-1.0]])]});}
            extrude(context, id + "F9", {"entities" : qUnion([Q0, Q1, Q2, Q3, Q4, Q5, Q6, Q7]), "operationType" : NewBodyOperationType.ADD, "oppositeDirection" : true, "depth" : 3 * mm, "offsetDistance" : 25 * mm});
        }
        {
            var Q0;
            Q0=makeQuery(id+"F9.opExtrude","CAP_FACE",FACE,{"disambiguationData":[OSD([sQuery(id+"F0.wireOp",EDGE,"E9")])],"isStart":false});
            var Q1;
            Q1=makeQuery(id+"F9.opExtrude","CAP_FACE",FACE,{"disambiguationData":[OSD([sQuery(id+"F0.wireOp",EDGE,"E8")])],"isStart":false});
            chamfer(context, id + "F10", {"entities" : qUnion([Q0, Q1]), "width" : 2 * mm, "tangentPropagation" : true});
        }
        {
            var Q0;
            Q0=qCreatedBy(makeId("Front.planeOp"),FACE);
            var sketch = newSketch(context, id + "F11", { "sketchPlane" : qUnion([Q0])});
            skLineSegment(sketch, "E19", {"start": v(0, 0) * mm, "end": v(0, 25) * mm});
            skLineSegment(sketch, "E20.bottom", {"start": v(-19.86, 45) * mm, "end": v(19.86, 45) * mm});
            skLineSegment(sketch, "E20.top", {"start": v(-19.86, 5) * mm, "end": v(19.86, 5) * mm});
            skLineSegment(sketch, "E20.left", {"start": v(-19.86, 45) * mm, "end": v(-19.86, 5) * mm});
            skLineSegment(sketch, "E20.right", {"start": v(19.86, 45) * mm, "end": v(19.86, 5) * mm});
            skPoint(sketch, "E20.middle", {"position": v(0, 25) * mm});
            skSolve(sketch);
        }
        {
            var Q0;
            Q0=qSketchRegion(id+"F11",true);
            extrude(context, id + "F12", {"entities" : qUnion([Q0]), "operationType" : NewBodyOperationType.REMOVE, "endBound" : BoundingType.SYMMETRIC, "depth" : 40 * mm, "offsetDistance" : 25 * mm});
        }
    });
